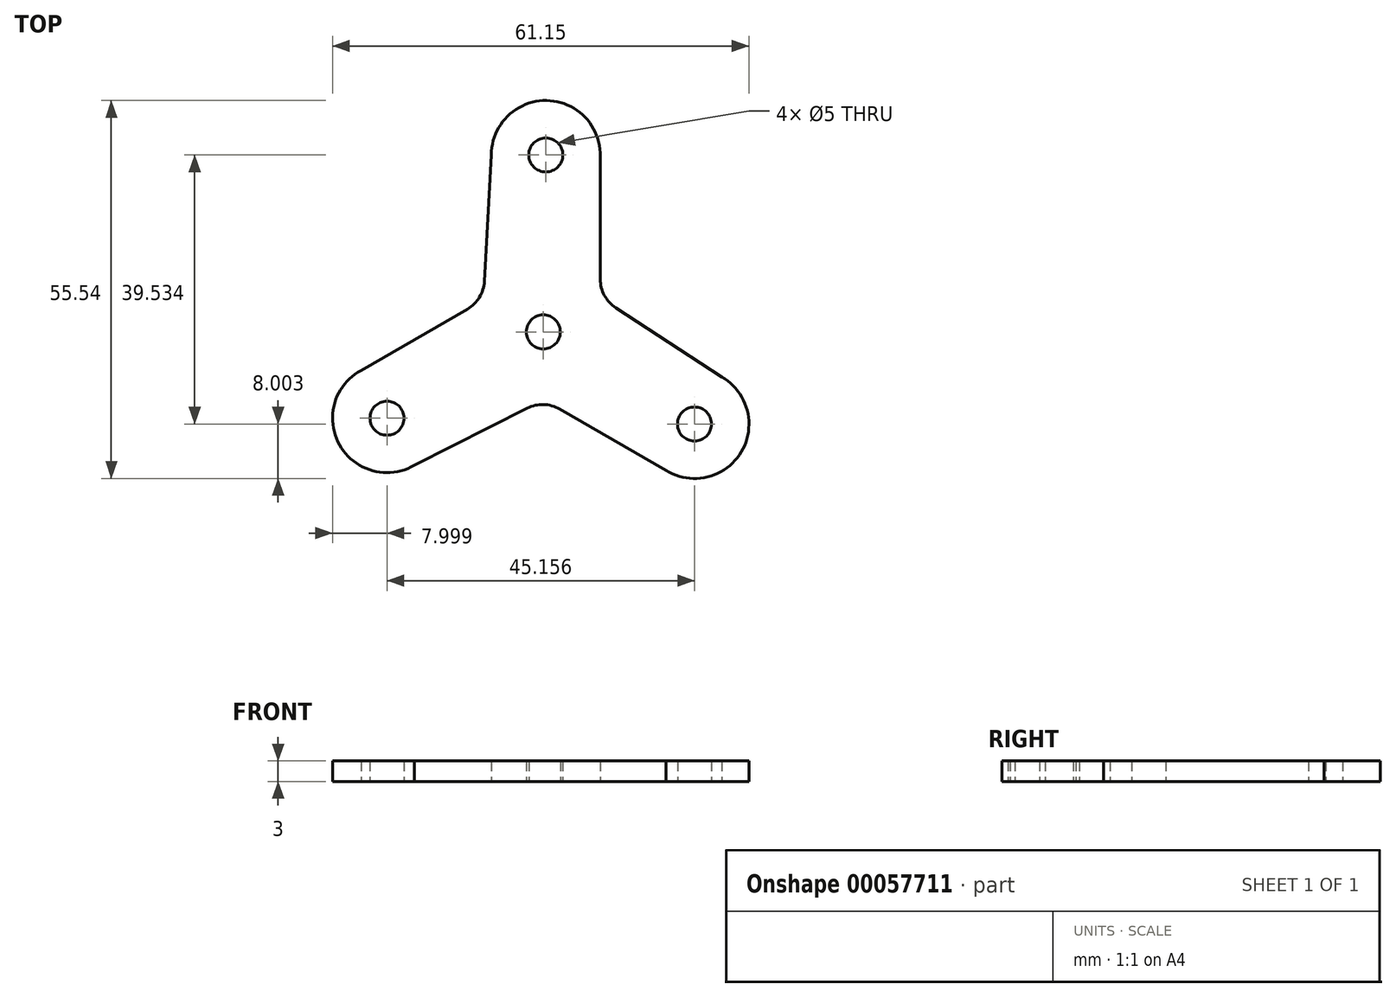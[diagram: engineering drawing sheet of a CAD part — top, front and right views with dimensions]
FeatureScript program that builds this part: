
annotation { "Feature Type Name" : "Feature", "Feature Type Description" : "" }
export const myFeature = defineFeature(function(context is Context, id is Id, definition is map)
    precondition{}
    {
        {
            var Q0;
            Q0=qCreatedBy(makeId("Top.planeOp"),FACE);
            var sketch = newSketch(context, id + "F0", { "sketchPlane" : qUnion([Q0])});
            skCircle(sketch, "E0", {"center": v(0, 0) * mm, "radius": 2.5 * mm});
            skCircle(sketch, "E1", {"center": v(0.37, 26) * mm, "radius": 2.5 * mm});
            skLineSegment(sketch, "E2", {"start": v(0.37, 26) * mm, "end": v(0, 0) * mm});
            skArc(sketch, "E3", {"start": v(8.37, 25.78) * mm, "mid": v(0.48, 34) * mm, "end": v(-7.63, 26) * mm});
            skCircle(sketch, "E4", {"center": v(0, 0) * mm, "radius": 9 * mm});
            skLineSegment(sketch, "E5", {"start": v(-8.65, 7.43) * mm, "end": v(-7.63, 26) * mm});
            skLineSegment(sketch, "E6", {"start": v(8.37, 25.78) * mm, "end": v(8.37, 7.75) * mm});
            skLineSegment(sketch, "E7.1.0", {"start": v(-2.36, -11.2) * mm, "end": v(-18.95, -19.6) * mm});
            skArc(sketch, "E7.1.1", {"start": v(-26.76, -5.65) * mm, "mid": v(-29.93, -16.59) * mm, "end": v(-18.95, -19.6) * mm});
            skLineSegment(sketch, "E7.1.2", {"start": v(-26.76, -5.65) * mm, "end": v(-11.15, 3.37) * mm});
            skCircle(sketch, "E7.1.3", {"center": v(-22.95, -12.68) * mm, "radius": 2.5 * mm});
            skLineSegment(sketch, "E7.1.4", {"start": v(-22.95, -12.68) * mm, "end": v(-0.25, 0) * mm});
            skLineSegment(sketch, "E7.2.0", {"start": v(10.63, 3.56) * mm, "end": v(26.2, -6.6) * mm});
            skArc(sketch, "E7.2.1", {"start": v(18.02, -20.35) * mm, "mid": v(29.08, -17.63) * mm, "end": v(26.2, -6.6) * mm});
            skLineSegment(sketch, "E7.2.2", {"start": v(18.02, -20.35) * mm, "end": v(2.4, -11.34) * mm});
            skCircle(sketch, "E7.2.3", {"center": v(22.2, -13.54) * mm, "radius": 2.5 * mm});
            skLineSegment(sketch, "E7.2.4", {"start": v(22.2, -13.54) * mm, "end": v(-0.13, -0.22) * mm});
            skPoint(sketch, "E7.center", {"position": v(-0.13, -0.07) * mm});
            skPoint(sketch, "E8.newPointA", {"position": v(-4.44, 7.24) * mm});
            skPoint(sketch, "E8.newPointB", {"position": v(-9.06, 0) * mm});
            skArc(sketch, "E8.filletArc", {"start": v(-11.15, 3.37) * mm, "mid": v(-9.39, 5.08) * mm, "end": v(-8.65, 7.43) * mm});
            skArc(sketch, "E9.1.0", {"start": v(2.4, -11.34) * mm, "mid": v(0.04, -10.67) * mm, "end": v(-2.36, -11.2) * mm});
            skArc(sketch, "E9.2.0", {"start": v(8.37, 7.75) * mm, "mid": v(8.97, 5.37) * mm, "end": v(10.63, 3.56) * mm});
            skPoint(sketch, "E10.orphan", {"position": v(8.37, 0) * mm});
            skPoint(sketch, "E11.orphan", {"position": v(4.4, 7.63) * mm});
            skPoint(sketch, "E12.orphan", {"position": v(4.28, -7.85) * mm});
            skSolve(sketch);
        }
        {
            var Q0;
            Q0=makeQuery(id+"F0.imprint","IMPRINT",FACE,{"disambiguationData":[TD([[makeQuery(id+"F0.imprint","IMPRINT",EDGE,{"derivedFrom":sQuery(id+"F0.wireOp",EDGE,"E1")}),-1.0]])]});
            var Q1;
            {var subQ0=sQuery(id+"F0.wireOp",EDGE,"E7.1.4");var subQ1=sQuery(id+"F0.wireOp",EDGE,"E0");var subQ2=makeQuery(id+"F0.imprint","INTERSECT",VERTEX,{"derivedFrom":[subQ1,subQ0]});Q1=makeQuery(id+"F0.imprint","IMPRINT",FACE,{"disambiguationData":[TD([[makeQuery(id+"F0.imprint","IMPRINT",EDGE,{"disambiguationData":[TD([[subQ2,1.0]])],"derivedFrom":subQ1}),-1.0]])]});}
            var Q2;
            {var subQ2=sQuery(id+"F0.wireOp",EDGE,"E2");var subQ5=sQuery(id+"F0.wireOp",EDGE,"E0");var subQ6=makeQuery(id+"F0.imprint","INTERSECT",VERTEX,{"derivedFrom":[subQ5,subQ2]});Q2=makeQuery(id+"F0.imprint","IMPRINT",FACE,{"disambiguationData":[TD([[makeQuery(id+"F0.imprint","IMPRINT",EDGE,{"disambiguationData":[TD([[subQ6,1.0]])],"derivedFrom":subQ5}),-1.0]])]});}
            var Q3;
            {var subQ5=sQuery(id+"F0.wireOp",EDGE,"E0");var subQ7=sQuery(id+"F0.wireOp",EDGE,"E7.1.4");var subQ9=makeQuery(id+"F0.imprint","INTERSECT",VERTEX,{"derivedFrom":[subQ5,subQ7]});Q3=makeQuery(id+"F0.imprint","IMPRINT",FACE,{"disambiguationData":[TD([[makeQuery(id+"F0.imprint","IMPRINT",EDGE,{"disambiguationData":[TD([[subQ9,-1.0]])],"derivedFrom":subQ5}),-1.0]])]});}
            var Q4;
            {var subQ12=sQuery(id+"F0.wireOp",EDGE,"E7.2.1");Q4=makeQuery(id+"F0.imprint","IMPRINT",FACE,{"disambiguationData":[TD([[makeQuery(id+"F0.imprint","IMPRINT",EDGE,{"derivedFrom":subQ12}),1.0]])]});}
            var Q5;
            {var subQ0=sQuery(id+"F0.wireOp",EDGE,"E7.1.0");var subQ1=sQuery(id+"F0.wireOp",EDGE,"E4");var subQ2=makeQuery(id+"F0.imprint","INTERSECT",VERTEX,{"derivedFrom":[subQ1,subQ0]});Q5=makeQuery(id+"F0.imprint","IMPRINT",FACE,{"disambiguationData":[TD([[makeQuery(id+"F0.imprint","IMPRINT",EDGE,{"disambiguationData":[TD([[subQ2,1.0]])],"derivedFrom":subQ1}),-1.0]])]});}
            var Q6;
            {var subQ0=sQuery(id+"F0.wireOp",EDGE,"E6");var subQ1=sQuery(id+"F0.wireOp",EDGE,"E4");var subQ2=makeQuery(id+"F0.imprint","INTERSECT",VERTEX,{"derivedFrom":[subQ1,subQ0]});Q6=makeQuery(id+"F0.imprint","IMPRINT",FACE,{"disambiguationData":[TD([[makeQuery(id+"F0.imprint","IMPRINT",EDGE,{"disambiguationData":[TD([[subQ2,-1.0]])],"derivedFrom":subQ1}),-1.0]])]});}
            var Q7;
            {var subQ0=sQuery(id+"F0.wireOp",EDGE,"E9.2.0");Q7=makeQuery(id+"F0.imprint","IMPRINT",FACE,{"disambiguationData":[TD([[makeQuery(id+"F0.imprint","IMPRINT",EDGE,{"derivedFrom":subQ0}),-1.0]])]});}
            var Q8;
            {var subQ0=sQuery(id+"F0.wireOp",EDGE,"E9.1.0");Q8=makeQuery(id+"F0.imprint","IMPRINT",FACE,{"disambiguationData":[TD([[makeQuery(id+"F0.imprint","IMPRINT",EDGE,{"derivedFrom":subQ0}),-1.0]])]});}
            extrude(context, id + "F1", {"entities" : qUnion([Q0, Q1, Q2, Q3, Q4, Q5, Q6, Q7, Q8]), "depth" : 3 * mm});
        }
    });
